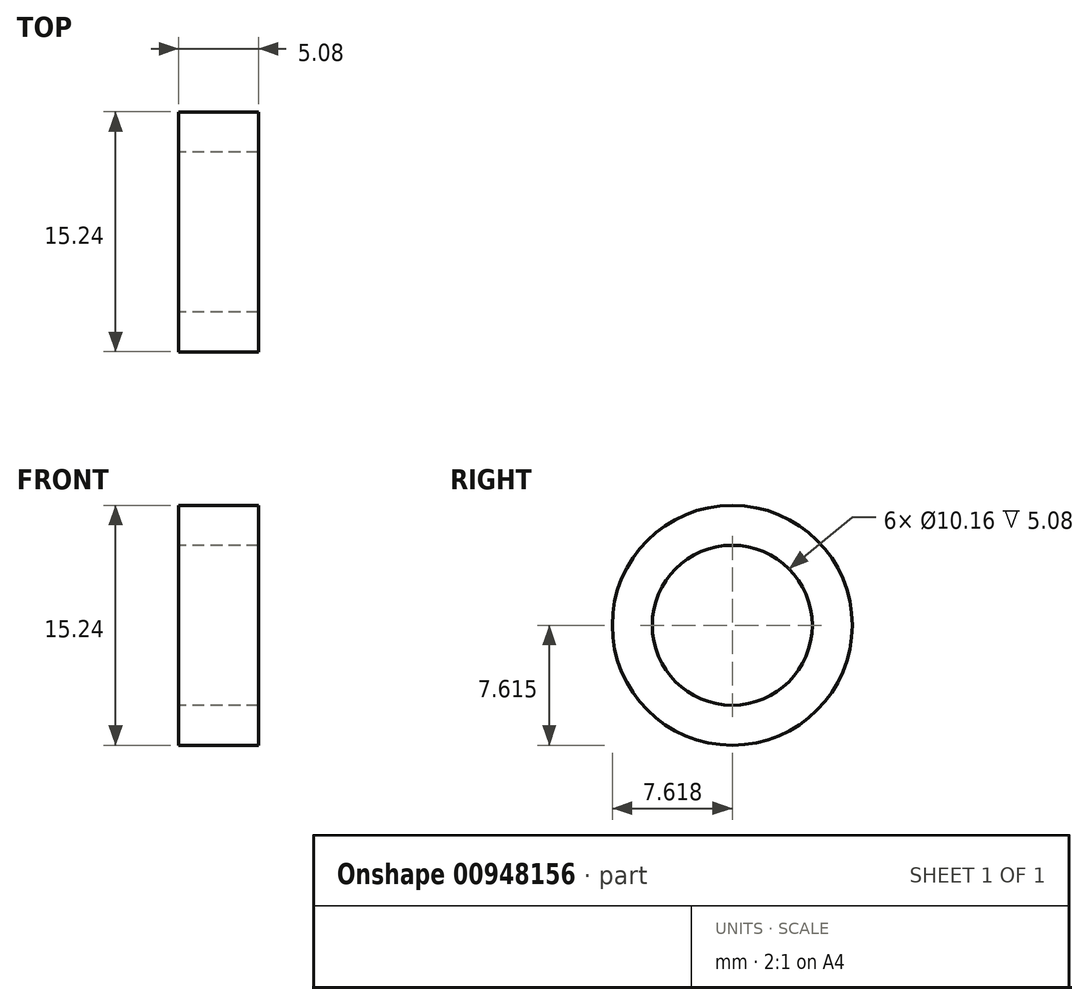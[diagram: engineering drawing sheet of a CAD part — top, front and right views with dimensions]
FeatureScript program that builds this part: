
annotation { "Feature Type Name" : "Feature", "Feature Type Description" : "" }
export const myFeature = defineFeature(function(context is Context, id is Id, definition is map)
    precondition{}
    {
        {
            var Q0;
            Q0=qCreatedBy(makeId("Right.planeOp"),FACE);
            var sketch = newSketch(context, id + "F0", { "sketchPlane" : qUnion([Q0])});
            skCircle(sketch, "E0", {"center": v(-6.01, 19.24) * mm, "radius": 7.62 * mm});
            skCircle(sketch, "E1", {"center": v(-6.01, 19.24) * mm, "radius": 5.08 * mm});
            skSolve(sketch);
        }
        {
            var Q0;
            Q0=makeQuery(id+"F0.imprint","IMPRINT",FACE,{"disambiguationData":[TD([[makeQuery(id+"F0.imprint","IMPRINT",EDGE,{"derivedFrom":sQuery(id+"F0.wireOp",EDGE,"E0")}),1.0]])]});
            extrude(context, id + "F1", {"entities" : qUnion([Q0]), "depth" : 5.08 * mm, "offsetDistance" : 25.4 * mm});
        }
    });
